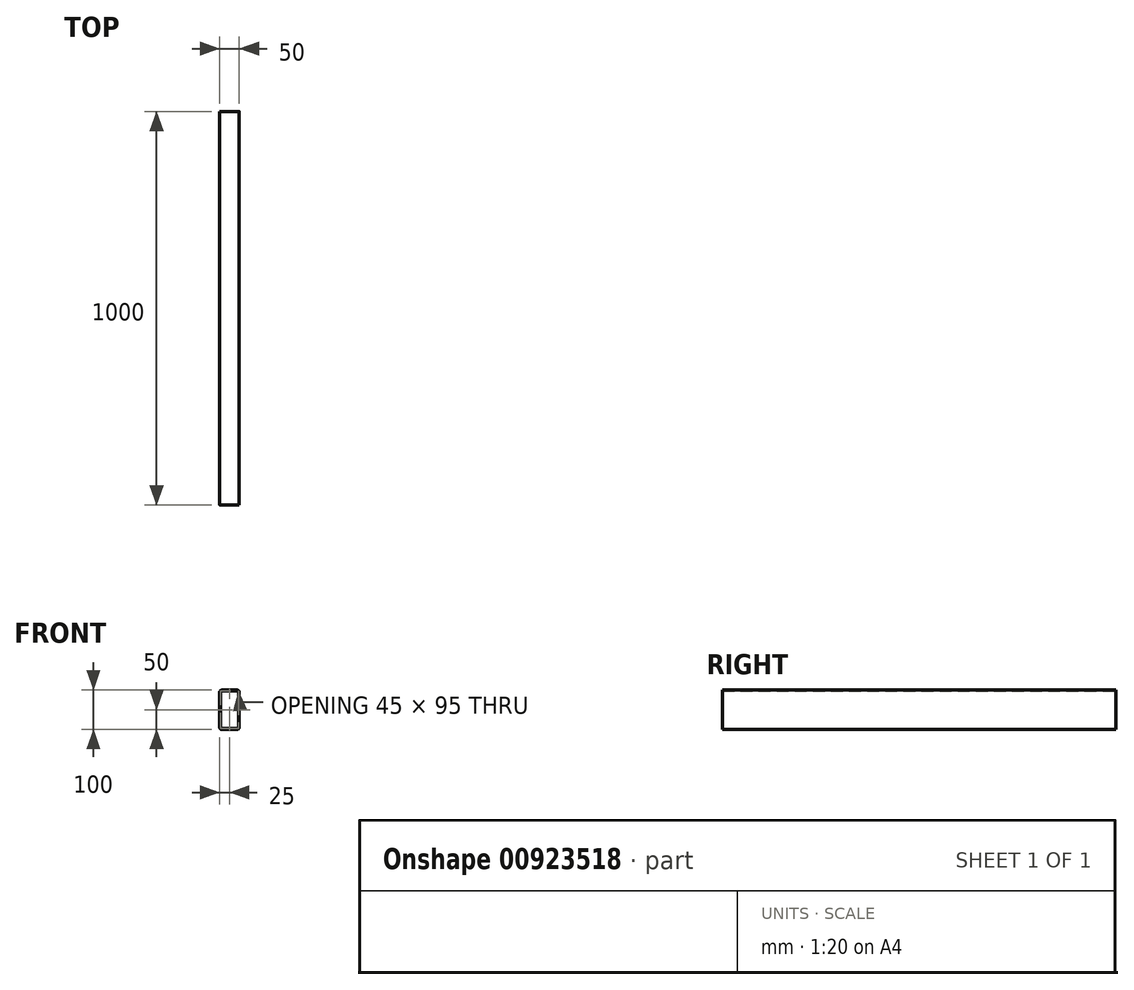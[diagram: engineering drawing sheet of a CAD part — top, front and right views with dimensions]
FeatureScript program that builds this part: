
annotation { "Feature Type Name" : "Feature", "Feature Type Description" : "" }
export const myFeature = defineFeature(function(context is Context, id is Id, definition is map)
    precondition{}
    {
        {
            var Q0;
            Q0=qCreatedBy(makeId("Front.planeOp"),FACE);
            var sketch = newSketch(context, id + "F0", { "sketchPlane" : qUnion([Q0])});
            skLineSegment(sketch, "E0.bottom", {"start": v(-25, 50) * mm, "end": v(25, 50) * mm});
            skLineSegment(sketch, "E0.top", {"start": v(-25, -50) * mm, "end": v(25, -50) * mm});
            skLineSegment(sketch, "E0.left", {"start": v(-25, 50) * mm, "end": v(-25, -50) * mm});
            skLineSegment(sketch, "E0.right", {"start": v(25, 50) * mm, "end": v(25, -50) * mm});
            skSolve(sketch);
        }
        {
            var Q0;
            Q0=makeQuery(id+"F0.imprint","IMPRINT",FACE,{"disambiguationData":[TD([[makeQuery(id+"F0.imprint","IMPRINT",EDGE,{"derivedFrom":sQuery(id+"F0.wireOp",EDGE,"E0.bottom")}),-1.0]])]});
            extrude(context, id + "F1", {"entities" : qUnion([Q0]), "depth" : 1000 * mm, "offsetDistance" : 25 * mm});
        }
        {
            var Q0;
            Q0=makeQuery(id+"F1.opExtrude","SWEPT_EDGE",EDGE,{"disambiguationData":[OSD([sQuery(id+"F0.wireOp",EDGE,"E0.bottom"),sQuery(id+"F0.wireOp",EDGE,"E0.left")])]});
            var Q1;
            Q1=makeQuery(id+"F1.opExtrude","SWEPT_EDGE",EDGE,{"disambiguationData":[OSD([sQuery(id+"F0.wireOp",EDGE,"E0.bottom"),sQuery(id+"F0.wireOp",EDGE,"E0.right")])]});
            var Q2;
            Q2=makeQuery(id+"F1.opExtrude","SWEPT_EDGE",EDGE,{"disambiguationData":[OSD([sQuery(id+"F0.wireOp",EDGE,"E0.top"),sQuery(id+"F0.wireOp",EDGE,"E0.right")])]});
            var Q3;
            Q3=makeQuery(id+"F1.opExtrude","SWEPT_EDGE",EDGE,{"disambiguationData":[OSD([sQuery(id+"F0.wireOp",EDGE,"E0.top"),sQuery(id+"F0.wireOp",EDGE,"E0.left")])]});
            fillet(context, id + "F2", {"entities" : qUnion([Q0, Q1, Q2, Q3]), "radius" : 5.5 * mm, "tangentPropagation" : true, "allowEdgeOverflow" : false});
        }
        {
            var Q0;
            Q0=makeQuery(id+"F1.opExtrude","CAP_FACE",FACE,{"disambiguationData":[OSD([sQuery(id+"F0.wireOp",EDGE,"E0.bottom"),sQuery(id+"F0.wireOp",EDGE,"E0.top"),sQuery(id+"F0.wireOp",EDGE,"E0.left"),sQuery(id+"F0.wireOp",EDGE,"E0.right")])],"isStart":false});
            var Q1;
            Q1=makeQuery(id+"F1.opExtrude","CAP_FACE",FACE,{"disambiguationData":[OSD([sQuery(id+"F0.wireOp",EDGE,"E0.bottom"),sQuery(id+"F0.wireOp",EDGE,"E0.top"),sQuery(id+"F0.wireOp",EDGE,"E0.left"),sQuery(id+"F0.wireOp",EDGE,"E0.right")])],"isStart":true});
            shell(context, id + "F3", {"entities" : qUnion([Q0, Q1]), "thickness" : 2.5 * mm});
        }
    });
